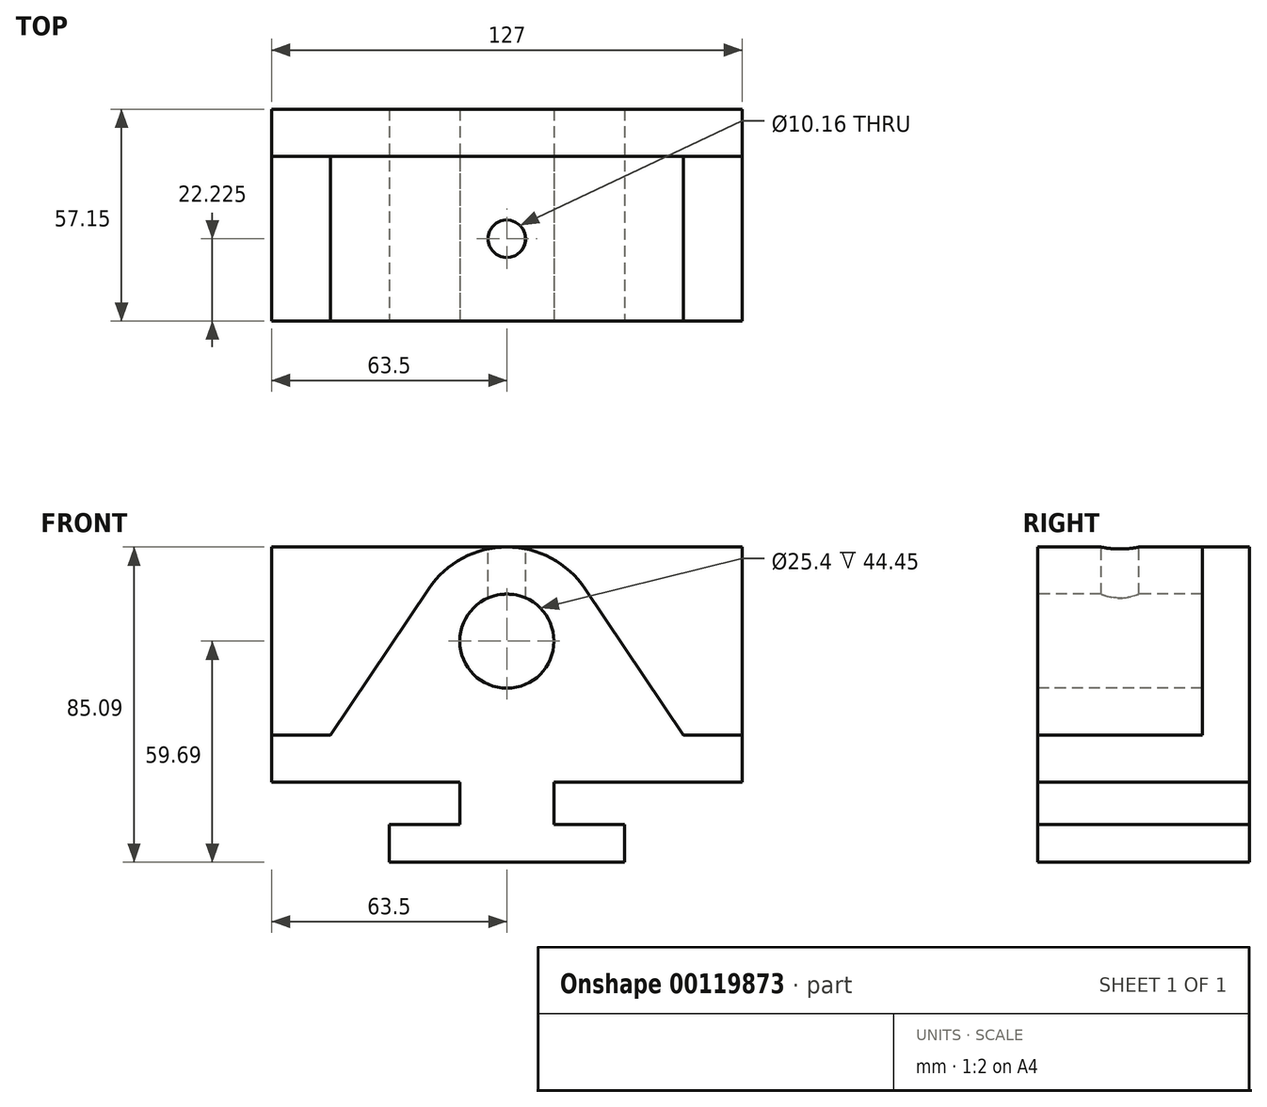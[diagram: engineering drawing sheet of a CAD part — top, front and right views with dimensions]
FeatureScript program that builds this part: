
annotation { "Feature Type Name" : "Feature", "Feature Type Description" : "" }
export const myFeature = defineFeature(function(context is Context, id is Id, definition is map)
    precondition{}
    {
        {
            var Q0;
            Q0=qCreatedBy(makeId("Front.planeOp"),FACE);
            var sketch = newSketch(context, id + "F0", { "sketchPlane" : qUnion([Q0])});
            skLineSegment(sketch, "E0.bottom", {"start": v(0, 0) * mm, "end": v(127, 0) * mm});
            skLineSegment(sketch, "E0.top", {"start": v(0, 63.5) * mm, "end": v(127, 63.5) * mm});
            skLineSegment(sketch, "E0.left", {"start": v(0, 0) * mm, "end": v(0, 63.5) * mm});
            skLineSegment(sketch, "E0.right", {"start": v(127, 0) * mm, "end": v(127, 63.5) * mm});
            skSolve(sketch);
        }
        {
            var Q0;
            Q0 = qSketchRegion(id + "F0", true);
            extrude(context, id + "F1", {"entities" : qUnion([Q0]), "depth" : 12.7 * mm});
        }
        {
            var Q0;
            Q0=makeQuery(id+"F1.opExtrude","CAP_FACE",FACE,{"disambiguationData":[OSD([sQuery(id+"F0.wireOp",EDGE,"E0.bottom"),sQuery(id+"F0.wireOp",EDGE,"E0.top"),sQuery(id+"F0.wireOp",EDGE,"E0.left"),sQuery(id+"F0.wireOp",EDGE,"E0.right")])],"isStart":false});
            var sketch = newSketch(context, id + "F2", { "sketchPlane" : qUnion([Q0])});
            skLineSegment(sketch, "E1.bottom", {"start": v(0, 0) * mm, "end": v(127, 0) * mm});
            skLineSegment(sketch, "E1.top", {"start": v(0, 12.7) * mm, "end": v(127, 12.7) * mm});
            skLineSegment(sketch, "E1.left", {"start": v(0, 0) * mm, "end": v(0, 12.7) * mm});
            skLineSegment(sketch, "E1.right", {"start": v(127, 0) * mm, "end": v(127, 12.7) * mm});
            skSolve(sketch);
        }
        {
            var Q0;
            Q0=makeQuery(id+"F2.imprint","IMPRINT",FACE,{"disambiguationData":[TD([[makeQuery(id+"F2.imprint","IMPRINT",EDGE,{"derivedFrom":sQuery(id+"F2.wireOp",EDGE,"E1.bottom")}),1.0]])]});
            extrude(context, id + "F3", {"entities" : qUnion([Q0]), "operationType" : NewBodyOperationType.ADD, "depth" : 44.45 * mm});
        }
        {
            var Q0;
            Q0=makeQuery(id+"F3.opExtrude","CAP_FACE",FACE,{"disambiguationData":[OSD([sQuery(id+"F2.wireOp",EDGE,"E1.bottom"),sQuery(id+"F2.wireOp",EDGE,"E1.top"),sQuery(id+"F2.wireOp",EDGE,"E1.left"),sQuery(id+"F2.wireOp",EDGE,"E1.right")])],"isStart":false});
            var sketch = newSketch(context, id + "F4", { "sketchPlane" : qUnion([Q0])});
            skLineSegment(sketch, "E2", {"start": v(0, 0) * mm, "end": v(127, 0) * mm, "construction": true});
            skLineSegment(sketch, "E3", {"start": v(127, 0) * mm, "end": v(63.5, 0) * mm, "construction": true});
            skLineSegment(sketch, "E4", {"start": v(63.5, 0) * mm, "end": v(0, 0) * mm, "construction": true});
            skLineSegment(sketch, "E5", {"start": v(63.5, 0) * mm, "end": v(63.5, 63.5) * mm, "construction": true});
            skPoint(sketch, "E5.endSnap0", {"position": v(63.5, 12.7) * mm});
            skLineSegment(sketch, "E6", {"start": v(63.5, 63.5) * mm, "end": v(63.5, 0) * mm, "construction": true});
            skLineSegment(sketch, "E7", {"start": v(63.5, 0) * mm, "end": v(63.5, -21.59) * mm, "construction": true});
            skLineSegment(sketch, "E8", {"start": v(63.5, -21.59) * mm, "end": v(31.75, -21.59) * mm});
            skLineSegment(sketch, "E9", {"start": v(31.75, -21.6) * mm, "end": v(31.75, -11.38) * mm});
            skLineSegment(sketch, "E10", {"start": v(31.75, -11.38) * mm, "end": v(50.8, -11.38) * mm});
            skLineSegment(sketch, "E11", {"start": v(50.8, -11.38) * mm, "end": v(50.8, 0) * mm});
            skLineSegment(sketch, "E12", {"start": v(50.8, 0) * mm, "end": v(63.5, 0) * mm});
            skLineSegment(sketch, "E13.MirrorCS", {"start": v(76.2, -11.38) * mm, "end": v(76.2, 0) * mm});
            skLineSegment(sketch, "E14.MirrorCS", {"start": v(63.5, -21.59) * mm, "end": v(95.25, -21.59) * mm});
            skLineSegment(sketch, "E15.MirrorCS", {"start": v(95.25, -11.38) * mm, "end": v(76.2, -11.38) * mm});
            skLineSegment(sketch, "E16.MirrorCS", {"start": v(95.25, -21.6) * mm, "end": v(95.25, -11.38) * mm});
            skSolve(sketch);
        }
        {
            var Q0;
            Q0=makeQuery(id+"F4.imprint","IMPRINT",FACE,{"disambiguationData":[TD([[makeQuery(id+"F4.imprint","IMPRINT",EDGE,{"derivedFrom":sQuery(id+"F4.wireOp",EDGE,"E8")}),-1.0]])]});
            extrude(context, id + "F5", {"entities" : qUnion([Q0]), "operationType" : NewBodyOperationType.ADD, "oppositeDirection" : true, "depth" : 57.15 * mm});
        }
        {
            var Q0;
            {var subQ0=sQuery(id+"F2.wireOp",EDGE,"E1.bottom");Q0=makeQuery(id+"F5.boolean.opBoolean","MERGE",FACE,{"derivedFrom":[makeQuery(id+"F3.opExtrude","CAP_FACE",FACE,{"disambiguationData":[OSD([subQ0,sQuery(id+"F2.wireOp",EDGE,"E1.top"),sQuery(id+"F2.wireOp",EDGE,"E1.left"),sQuery(id+"F2.wireOp",EDGE,"E1.right")])],"isStart":false}),makeQuery(id+"F5.opExtrude","CAP_FACE",FACE,{"disambiguationData":[OSD([subQ0,sQuery(id+"F4.wireOp",EDGE,"E8"),sQuery(id+"F4.wireOp",EDGE,"E9"),sQuery(id+"F4.wireOp",EDGE,"E10"),sQuery(id+"F4.wireOp",EDGE,"E11"),sQuery(id+"F4.wireOp",EDGE,"E12"),sQuery(id+"F4.wireOp",EDGE,"E13.MirrorCS"),sQuery(id+"F4.wireOp",EDGE,"E14.MirrorCS"),sQuery(id+"F4.wireOp",EDGE,"E15.MirrorCS"),sQuery(id+"F4.wireOp",EDGE,"E16.MirrorCS")])],"isStart":true})]});}
            var sketch = newSketch(context, id + "F6", { "sketchPlane" : qUnion([Q0])});
            skLineSegment(sketch, "E17", {"start": v(0, 12.7) * mm, "end": v(15.87, 12.7) * mm});
            skLineSegment(sketch, "E18", {"start": v(127, 12.7) * mm, "end": v(111.12, 12.7) * mm});
            skLineSegment(sketch, "E19", {"start": v(15.87, 12.7) * mm, "end": v(111.12, 12.7) * mm, "construction": true});
            skLineSegment(sketch, "E20", {"start": v(63.5, 12.7) * mm, "end": v(63.5, 63.5) * mm, "construction": true});
            skPoint(sketch, "E20.endSnap0", {"position": v(63.5, 12.7) * mm});
            skLineSegment(sketch, "E21", {"start": v(15.87, 12.7) * mm, "end": v(42.4, 52.25) * mm});
            skLineSegment(sketch, "E22", {"start": v(111.13, 12.7) * mm, "end": v(84.6, 52.25) * mm});
            skArc(sketch, "E23", {"start": v(84.6, 52.25) * mm, "mid": v(63.5, 63.5) * mm, "end": v(42.4, 52.25) * mm});
            skLineSegment(sketch, "E24", {"start": v(15.87, 12.7) * mm, "end": v(111.12, 12.7) * mm});
            skCircle(sketch, "E25", {"center": v(63.5, 38.1) * mm, "radius": 12.7 * mm});
            skSolve(sketch);
        }
        {
            var Q0;
            Q0=makeQuery(id+"F6.imprint","IMPRINT",FACE,{"disambiguationData":[TD([[makeQuery(id+"F6.imprint","IMPRINT",EDGE,{"derivedFrom":sQuery(id+"F6.wireOp",EDGE,"E21")}),-1.0]])]});
            extrude(context, id + "F7", {"entities" : qUnion([Q0]), "operationType" : NewBodyOperationType.ADD, "oppositeDirection" : true, "depth" : 44.45 * mm});
        }
        {
            var Q0;
            Q0=makeQuery(id+"F1.opExtrude","SWEPT_FACE",FACE,{"disambiguationData":[OSD([sQuery(id+"F0.wireOp",EDGE,"E0.top")])]});
            var sketch = newSketch(context, id + "F8", { "sketchPlane" : qUnion([Q0])});
            skLineSegment(sketch, "E26", {"start": v(0, 0) * mm, "end": v(127, 0) * mm, "construction": true});
            skLineSegment(sketch, "E27", {"start": v(127, 0) * mm, "end": v(63.5, 0) * mm, "construction": true});
            skLineSegment(sketch, "E28", {"start": v(63.5, 0) * mm, "end": v(63.5, -34.93) * mm, "construction": true});
            skCircle(sketch, "E29", {"center": v(63.5, -34.93) * mm, "radius": 5.08 * mm});
            skSolve(sketch);
        }
        {
            var Q0;
            Q0 = qSketchRegion(id + "F8", true);
            extrude(context, id + "F9", {"entities" : qUnion([Q0]), "operationType" : NewBodyOperationType.REMOVE, "oppositeDirection" : true, "depth" : 25.4 * mm});
        }
    });
